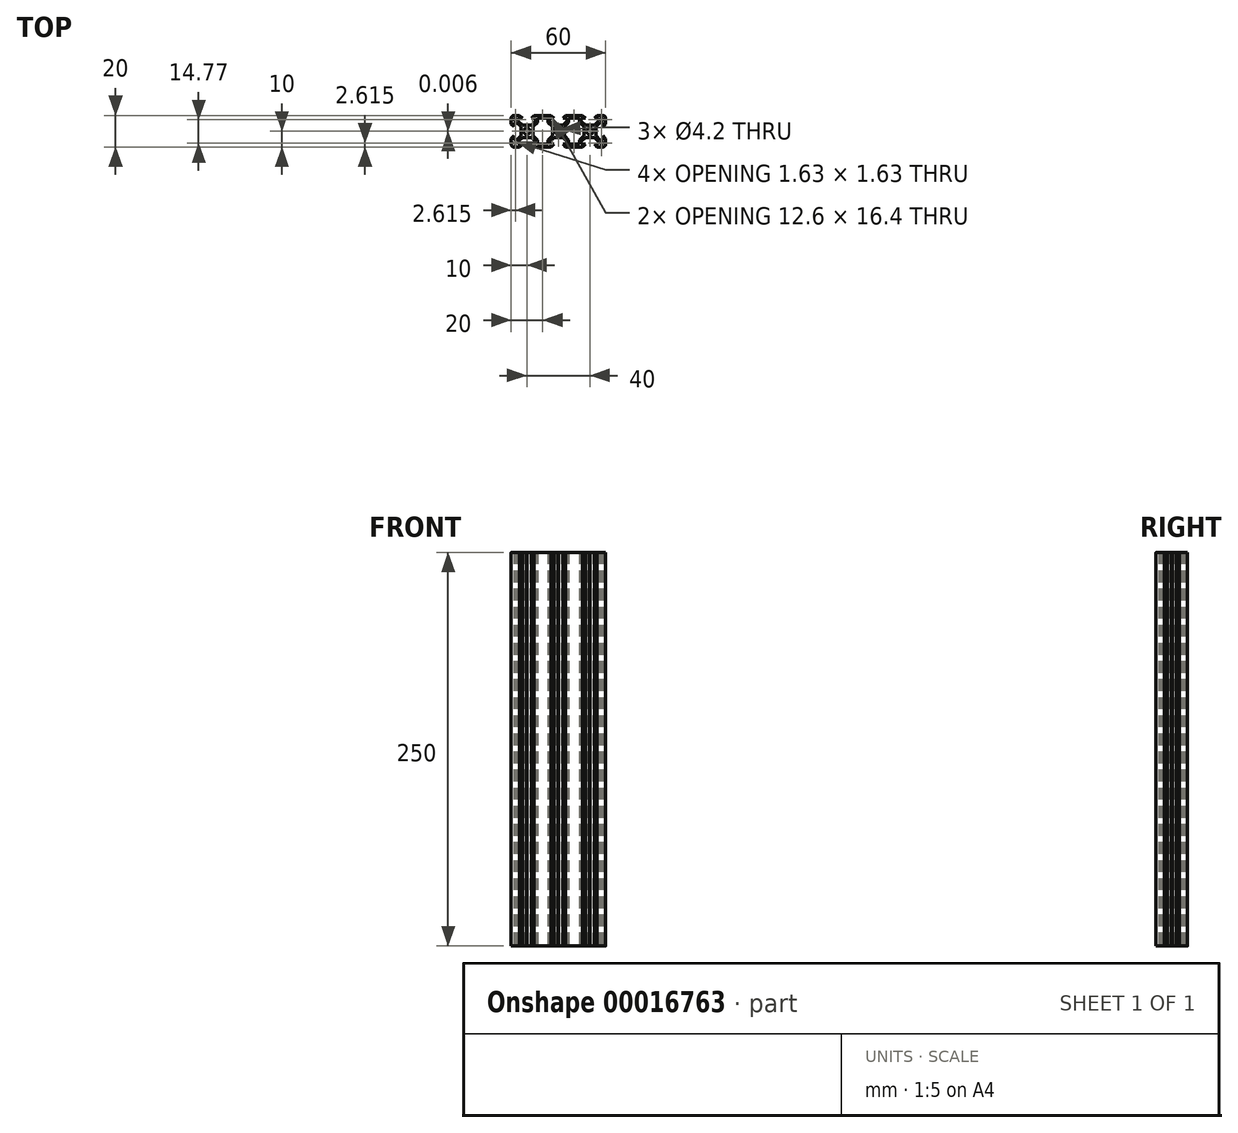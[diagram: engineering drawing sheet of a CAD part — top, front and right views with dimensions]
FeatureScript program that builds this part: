
annotation { "Feature Type Name" : "Feature", "Feature Type Description" : "" }
export const myFeature = defineFeature(function(context is Context, id is Id, definition is map)
    precondition{}
    {
        {
            var Q0;
            Q0=qCreatedBy(makeId("Top.planeOp"),FACE);
            var sketch = newSketch(context, id + "F0", { "sketchPlane" : qUnion([Q0])});
            skCircle(sketch, "E0", {"center": v(20, 0) * mm, "radius": 2.1 * mm});
            skLineSegment(sketch, "E1", {"start": v(-16.1, -2.84) * mm, "end": v(-13.43, -5.5) * mm});
            skLineSegment(sketch, "E2", {"start": v(-16.1, -0.2) * mm, "end": v(-16.1, -2.84) * mm});
            skLineSegment(sketch, "E3", {"start": v(-16.3, 0) * mm, "end": v(-16.1, -0.2) * mm});
            skLineSegment(sketch, "E4", {"start": v(-16.1, 0.2) * mm, "end": v(-16.3, 0) * mm});
            skLineSegment(sketch, "E5", {"start": v(-16.1, 2.84) * mm, "end": v(-16.1, 0.2) * mm});
            skLineSegment(sketch, "E6", {"start": v(-13.43, 5.5) * mm, "end": v(-16.1, 2.84) * mm});
            skLineSegment(sketch, "E7", {"start": v(-13.43, 8.2) * mm, "end": v(-13.43, 5.5) * mm});
            skLineSegment(sketch, "E8", {"start": v(-6.57, 8.2) * mm, "end": v(-13.43, 8.2) * mm});
            skLineSegment(sketch, "E9", {"start": v(-6.57, 5.5) * mm, "end": v(-6.57, 8.2) * mm});
            skLineSegment(sketch, "E10", {"start": v(-3.9, 2.84) * mm, "end": v(-6.57, 5.5) * mm});
            skLineSegment(sketch, "E11", {"start": v(-3.9, 0.2) * mm, "end": v(-3.9, 2.84) * mm});
            skLineSegment(sketch, "E12", {"start": v(-3.7, 0) * mm, "end": v(-3.9, 0.2) * mm});
            skLineSegment(sketch, "E13", {"start": v(-3.9, -0.2) * mm, "end": v(-3.7, 0) * mm});
            skLineSegment(sketch, "E14", {"start": v(-3.9, -2.84) * mm, "end": v(-3.9, -0.2) * mm});
            skLineSegment(sketch, "E15", {"start": v(-6.57, -5.5) * mm, "end": v(-3.9, -2.84) * mm});
            skLineSegment(sketch, "E16", {"start": v(-6.57, -8.2) * mm, "end": v(-6.57, -5.5) * mm});
            skLineSegment(sketch, "E17", {"start": v(-13.43, -8.2) * mm, "end": v(-6.57, -8.2) * mm});
            skLineSegment(sketch, "E18", {"start": v(-13.43, -5.5) * mm, "end": v(-13.43, -8.2) * mm});
            skLineSegment(sketch, "E19", {"start": v(26.57, 7.66) * mm, "end": v(27.66, 6.57) * mm});
            skLineSegment(sketch, "E20", {"start": v(26.57, 8.2) * mm, "end": v(26.57, 7.66) * mm});
            skLineSegment(sketch, "E21", {"start": v(28.2, 8.2) * mm, "end": v(26.57, 8.2) * mm});
            skLineSegment(sketch, "E22", {"start": v(28.2, 6.57) * mm, "end": v(28.2, 8.2) * mm});
            skLineSegment(sketch, "E23", {"start": v(27.66, 6.57) * mm, "end": v(28.2, 6.57) * mm});
            skLineSegment(sketch, "E24", {"start": v(27.66, -6.57) * mm, "end": v(26.57, -7.66) * mm});
            skLineSegment(sketch, "E25", {"start": v(28.2, -6.57) * mm, "end": v(27.66, -6.57) * mm});
            skLineSegment(sketch, "E26", {"start": v(28.2, -8.2) * mm, "end": v(28.2, -6.57) * mm});
            skLineSegment(sketch, "E27", {"start": v(26.57, -8.2) * mm, "end": v(28.2, -8.2) * mm});
            skLineSegment(sketch, "E28", {"start": v(26.57, -7.66) * mm, "end": v(26.57, -8.2) * mm});
            skLineSegment(sketch, "E29", {"start": v(-26.57, -7.66) * mm, "end": v(-27.66, -6.57) * mm});
            skLineSegment(sketch, "E30", {"start": v(-26.57, -8.2) * mm, "end": v(-26.57, -7.66) * mm});
            skLineSegment(sketch, "E31", {"start": v(-28.2, -8.2) * mm, "end": v(-26.57, -8.2) * mm});
            skLineSegment(sketch, "E32", {"start": v(-28.2, -6.57) * mm, "end": v(-28.2, -8.2) * mm});
            skLineSegment(sketch, "E33", {"start": v(-27.66, -6.57) * mm, "end": v(-28.2, -6.57) * mm});
            skLineSegment(sketch, "E34", {"start": v(-27.66, 6.57) * mm, "end": v(-26.57, 7.66) * mm});
            skLineSegment(sketch, "E35", {"start": v(-28.2, 6.57) * mm, "end": v(-27.66, 6.57) * mm});
            skLineSegment(sketch, "E36", {"start": v(-28.2, 8.2) * mm, "end": v(-28.2, 6.57) * mm});
            skLineSegment(sketch, "E37", {"start": v(-26.57, 8.2) * mm, "end": v(-28.2, 8.2) * mm});
            skLineSegment(sketch, "E38", {"start": v(-26.57, 7.66) * mm, "end": v(-26.57, 8.2) * mm});
            skLineSegment(sketch, "E39", {"start": v(-25.5, 8.2) * mm, "end": v(-22.84, 8.2) * mm});
            skLineSegment(sketch, "E40", {"start": v(-22.84, 8.2) * mm, "end": v(-24.64, 10) * mm});
            skLineSegment(sketch, "E41", {"start": v(-24.64, 10) * mm, "end": v(-28.2, 10) * mm});
            skArc(sketch, "E42", {"start": v(-28.2, 10) * mm, "mid": v(-29.47, 9.47) * mm, "end": v(-30, 8.2) * mm});
            skLineSegment(sketch, "E43", {"start": v(-30, 8.2) * mm, "end": v(-30, 4.64) * mm});
            skLineSegment(sketch, "E44", {"start": v(-30, 4.64) * mm, "end": v(-28.2, 2.84) * mm});
            skLineSegment(sketch, "E45", {"start": v(-28.2, 2.84) * mm, "end": v(-28.2, 5.5) * mm});
            skLineSegment(sketch, "E46", {"start": v(-28.2, 5.5) * mm, "end": v(-26.56, 5.5) * mm});
            skLineSegment(sketch, "E47", {"start": v(-26.56, 5.5) * mm, "end": v(-23.9, 2.84) * mm});
            skLineSegment(sketch, "E48", {"start": v(-23.9, 2.84) * mm, "end": v(-23.9, 0.2) * mm});
            skLineSegment(sketch, "E49", {"start": v(-23.9, 0.2) * mm, "end": v(-23.7, 0) * mm});
            skLineSegment(sketch, "E50", {"start": v(-23.7, 0) * mm, "end": v(-23.9, -0.2) * mm});
            skLineSegment(sketch, "E51", {"start": v(-23.9, -0.2) * mm, "end": v(-23.9, -2.84) * mm});
            skLineSegment(sketch, "E52", {"start": v(-23.9, -2.84) * mm, "end": v(-26.56, -5.5) * mm});
            skLineSegment(sketch, "E53", {"start": v(-26.56, -5.5) * mm, "end": v(-28.2, -5.5) * mm});
            skLineSegment(sketch, "E54", {"start": v(-28.2, -5.5) * mm, "end": v(-28.2, -2.84) * mm});
            skLineSegment(sketch, "E55", {"start": v(-28.2, -2.84) * mm, "end": v(-30, -4.64) * mm});
            skLineSegment(sketch, "E56", {"start": v(-30, -4.64) * mm, "end": v(-30, -8.2) * mm});
            skArc(sketch, "E57", {"start": v(-30, -8.2) * mm, "mid": v(-29.47, -9.47) * mm, "end": v(-28.2, -10) * mm});
            skLineSegment(sketch, "E58", {"start": v(-28.2, -10) * mm, "end": v(-24.64, -10) * mm});
            skLineSegment(sketch, "E59", {"start": v(-24.64, -10) * mm, "end": v(-22.84, -8.2) * mm});
            skLineSegment(sketch, "E60", {"start": v(-22.84, -8.2) * mm, "end": v(-25.5, -8.2) * mm});
            skLineSegment(sketch, "E61", {"start": v(-25.5, -8.2) * mm, "end": v(-25.5, -6.56) * mm});
            skLineSegment(sketch, "E62", {"start": v(-25.5, -6.56) * mm, "end": v(-22.84, -3.9) * mm});
            skLineSegment(sketch, "E63", {"start": v(-22.84, -3.9) * mm, "end": v(-20.2, -3.9) * mm});
            skLineSegment(sketch, "E64", {"start": v(-20.2, -3.9) * mm, "end": v(-20, -3.7) * mm});
            skLineSegment(sketch, "E65", {"start": v(-20, -3.7) * mm, "end": v(-19.8, -3.9) * mm});
            skLineSegment(sketch, "E66", {"start": v(-19.8, -3.9) * mm, "end": v(-17.16, -3.9) * mm});
            skLineSegment(sketch, "E67", {"start": v(-17.16, -3.9) * mm, "end": v(-14.5, -6.56) * mm});
            skLineSegment(sketch, "E68", {"start": v(-14.5, -6.56) * mm, "end": v(-14.5, -8.2) * mm});
            skLineSegment(sketch, "E69", {"start": v(-14.5, -8.2) * mm, "end": v(-17.16, -8.2) * mm});
            skLineSegment(sketch, "E70", {"start": v(-17.16, -8.2) * mm, "end": v(-15.36, -10) * mm});
            skLineSegment(sketch, "E71", {"start": v(-15.36, -10) * mm, "end": v(-4.64, -10) * mm});
            skLineSegment(sketch, "E72", {"start": v(-4.64, -10) * mm, "end": v(-2.84, -8.2) * mm});
            skLineSegment(sketch, "E73", {"start": v(-2.84, -8.2) * mm, "end": v(-5.5, -8.2) * mm});
            skLineSegment(sketch, "E74", {"start": v(-5.5, -8.2) * mm, "end": v(-5.5, -6.56) * mm});
            skLineSegment(sketch, "E75", {"start": v(-5.5, -6.56) * mm, "end": v(-2.84, -3.9) * mm});
            skLineSegment(sketch, "E76", {"start": v(-2.84, -3.9) * mm, "end": v(-0.2, -3.9) * mm});
            skLineSegment(sketch, "E77", {"start": v(-0.2, -3.9) * mm, "end": v(0, -3.7) * mm});
            skLineSegment(sketch, "E78", {"start": v(0, -3.7) * mm, "end": v(0.2, -3.9) * mm});
            skLineSegment(sketch, "E79", {"start": v(0.2, -3.9) * mm, "end": v(2.84, -3.9) * mm});
            skLineSegment(sketch, "E80", {"start": v(2.84, -3.9) * mm, "end": v(5.5, -6.56) * mm});
            skLineSegment(sketch, "E81", {"start": v(5.5, -6.56) * mm, "end": v(5.5, -8.2) * mm});
            skLineSegment(sketch, "E82", {"start": v(5.5, -8.2) * mm, "end": v(2.84, -8.2) * mm});
            skLineSegment(sketch, "E83", {"start": v(2.84, -8.2) * mm, "end": v(4.64, -10) * mm});
            skLineSegment(sketch, "E84", {"start": v(4.64, -10) * mm, "end": v(15.36, -10) * mm});
            skLineSegment(sketch, "E85", {"start": v(15.36, -10) * mm, "end": v(17.16, -8.2) * mm});
            skLineSegment(sketch, "E86", {"start": v(17.16, -8.2) * mm, "end": v(14.5, -8.2) * mm});
            skLineSegment(sketch, "E87", {"start": v(14.5, -8.2) * mm, "end": v(14.5, -6.56) * mm});
            skLineSegment(sketch, "E88", {"start": v(14.5, -6.56) * mm, "end": v(17.16, -3.9) * mm});
            skLineSegment(sketch, "E89", {"start": v(17.16, -3.9) * mm, "end": v(19.8, -3.9) * mm});
            skLineSegment(sketch, "E90", {"start": v(19.8, -3.9) * mm, "end": v(20, -3.7) * mm});
            skLineSegment(sketch, "E91", {"start": v(20, -3.7) * mm, "end": v(20.2, -3.9) * mm});
            skLineSegment(sketch, "E92", {"start": v(20.2, -3.9) * mm, "end": v(22.84, -3.9) * mm});
            skLineSegment(sketch, "E93", {"start": v(22.84, -3.9) * mm, "end": v(25.5, -6.56) * mm});
            skLineSegment(sketch, "E94", {"start": v(25.5, -6.56) * mm, "end": v(25.5, -8.2) * mm});
            skLineSegment(sketch, "E95", {"start": v(25.5, -8.2) * mm, "end": v(22.84, -8.2) * mm});
            skLineSegment(sketch, "E96", {"start": v(22.84, -8.2) * mm, "end": v(24.64, -10) * mm});
            skLineSegment(sketch, "E97", {"start": v(24.64, -10) * mm, "end": v(28.2, -10) * mm});
            skArc(sketch, "E98", {"start": v(28.2, -10) * mm, "mid": v(29.47, -9.47) * mm, "end": v(30, -8.2) * mm});
            skLineSegment(sketch, "E99", {"start": v(30, -8.2) * mm, "end": v(30, -4.64) * mm});
            skLineSegment(sketch, "E100", {"start": v(30, -4.64) * mm, "end": v(28.2, -2.84) * mm});
            skLineSegment(sketch, "E101", {"start": v(28.2, -2.84) * mm, "end": v(28.2, -5.5) * mm});
            skLineSegment(sketch, "E102", {"start": v(28.2, -5.5) * mm, "end": v(26.56, -5.5) * mm});
            skLineSegment(sketch, "E103", {"start": v(26.56, -5.5) * mm, "end": v(23.9, -2.84) * mm});
            skLineSegment(sketch, "E104", {"start": v(23.9, -2.84) * mm, "end": v(23.9, -0.2) * mm});
            skLineSegment(sketch, "E105", {"start": v(23.9, -0.2) * mm, "end": v(23.7, 0) * mm});
            skLineSegment(sketch, "E106", {"start": v(23.7, 0) * mm, "end": v(23.9, 0.2) * mm});
            skLineSegment(sketch, "E107", {"start": v(23.9, 0.2) * mm, "end": v(23.9, 2.84) * mm});
            skLineSegment(sketch, "E108", {"start": v(23.9, 2.84) * mm, "end": v(26.56, 5.5) * mm});
            skLineSegment(sketch, "E109", {"start": v(26.56, 5.5) * mm, "end": v(28.2, 5.5) * mm});
            skLineSegment(sketch, "E110", {"start": v(28.2, 5.5) * mm, "end": v(28.2, 2.84) * mm});
            skLineSegment(sketch, "E111", {"start": v(28.2, 2.84) * mm, "end": v(30, 4.64) * mm});
            skLineSegment(sketch, "E112", {"start": v(30, 4.64) * mm, "end": v(30, 8.2) * mm});
            skArc(sketch, "E113", {"start": v(30, 8.2) * mm, "mid": v(29.47, 9.47) * mm, "end": v(28.2, 10) * mm});
            skLineSegment(sketch, "E114", {"start": v(28.2, 10) * mm, "end": v(24.64, 10) * mm});
            skLineSegment(sketch, "E115", {"start": v(24.64, 10) * mm, "end": v(22.84, 8.2) * mm});
            skLineSegment(sketch, "E116", {"start": v(22.84, 8.2) * mm, "end": v(25.5, 8.2) * mm});
            skLineSegment(sketch, "E117", {"start": v(25.5, 8.2) * mm, "end": v(25.5, 6.56) * mm});
            skLineSegment(sketch, "E118", {"start": v(25.5, 6.56) * mm, "end": v(22.84, 3.9) * mm});
            skLineSegment(sketch, "E119", {"start": v(22.84, 3.9) * mm, "end": v(20.2, 3.9) * mm});
            skLineSegment(sketch, "E120", {"start": v(20.2, 3.9) * mm, "end": v(20, 3.7) * mm});
            skLineSegment(sketch, "E121", {"start": v(20, 3.7) * mm, "end": v(19.8, 3.9) * mm});
            skLineSegment(sketch, "E122", {"start": v(19.8, 3.9) * mm, "end": v(17.16, 3.9) * mm});
            skLineSegment(sketch, "E123", {"start": v(17.16, 3.9) * mm, "end": v(14.5, 6.56) * mm});
            skLineSegment(sketch, "E124", {"start": v(14.5, 6.56) * mm, "end": v(14.5, 8.2) * mm});
            skLineSegment(sketch, "E125", {"start": v(14.5, 8.2) * mm, "end": v(17.16, 8.2) * mm});
            skLineSegment(sketch, "E126", {"start": v(17.16, 8.2) * mm, "end": v(15.36, 10) * mm});
            skLineSegment(sketch, "E127", {"start": v(15.36, 10) * mm, "end": v(4.64, 10) * mm});
            skLineSegment(sketch, "E128", {"start": v(4.64, 10) * mm, "end": v(2.84, 8.2) * mm});
            skLineSegment(sketch, "E129", {"start": v(2.84, 8.2) * mm, "end": v(5.5, 8.2) * mm});
            skLineSegment(sketch, "E130", {"start": v(5.5, 8.2) * mm, "end": v(5.5, 6.56) * mm});
            skLineSegment(sketch, "E131", {"start": v(5.5, 6.56) * mm, "end": v(2.84, 3.9) * mm});
            skLineSegment(sketch, "E132", {"start": v(2.84, 3.9) * mm, "end": v(0.2, 3.9) * mm});
            skLineSegment(sketch, "E133", {"start": v(0.2, 3.9) * mm, "end": v(0, 3.7) * mm});
            skLineSegment(sketch, "E134", {"start": v(0, 3.7) * mm, "end": v(-0.2, 3.9) * mm});
            skLineSegment(sketch, "E135", {"start": v(-0.2, 3.9) * mm, "end": v(-2.84, 3.9) * mm});
            skLineSegment(sketch, "E136", {"start": v(-2.84, 3.9) * mm, "end": v(-5.5, 6.56) * mm});
            skLineSegment(sketch, "E137", {"start": v(-5.5, 6.56) * mm, "end": v(-5.5, 8.2) * mm});
            skLineSegment(sketch, "E138", {"start": v(-5.5, 8.2) * mm, "end": v(-2.84, 8.2) * mm});
            skLineSegment(sketch, "E139", {"start": v(-2.84, 8.2) * mm, "end": v(-4.64, 10) * mm});
            skLineSegment(sketch, "E140", {"start": v(-4.64, 10) * mm, "end": v(-15.36, 10) * mm});
            skLineSegment(sketch, "E141", {"start": v(-15.36, 10) * mm, "end": v(-17.16, 8.2) * mm});
            skLineSegment(sketch, "E142", {"start": v(-17.16, 8.2) * mm, "end": v(-14.5, 8.2) * mm});
            skLineSegment(sketch, "E143", {"start": v(-14.5, 8.2) * mm, "end": v(-14.5, 6.56) * mm});
            skLineSegment(sketch, "E144", {"start": v(-14.5, 6.56) * mm, "end": v(-17.16, 3.9) * mm});
            skLineSegment(sketch, "E145", {"start": v(-17.16, 3.9) * mm, "end": v(-19.8, 3.9) * mm});
            skLineSegment(sketch, "E146", {"start": v(-19.8, 3.9) * mm, "end": v(-20, 3.7) * mm});
            skLineSegment(sketch, "E147", {"start": v(-20, 3.7) * mm, "end": v(-20.2, 3.9) * mm});
            skLineSegment(sketch, "E148", {"start": v(-20.2, 3.9) * mm, "end": v(-22.84, 3.9) * mm});
            skLineSegment(sketch, "E149", {"start": v(-22.84, 3.9) * mm, "end": v(-25.5, 6.56) * mm});
            skLineSegment(sketch, "E150", {"start": v(-25.5, 6.56) * mm, "end": v(-25.5, 8.2) * mm});
            skCircle(sketch, "E151", {"center": v(-20, 0) * mm, "radius": 2.1 * mm});
            skLineSegment(sketch, "E152", {"start": v(16.1, 0.2) * mm, "end": v(16.1, 2.84) * mm});
            skLineSegment(sketch, "E153", {"start": v(16.3, 0) * mm, "end": v(16.1, 0.2) * mm});
            skLineSegment(sketch, "E154", {"start": v(16.1, -0.2) * mm, "end": v(16.3, 0) * mm});
            skLineSegment(sketch, "E155", {"start": v(16.1, -2.84) * mm, "end": v(16.1, -0.2) * mm});
            skLineSegment(sketch, "E156", {"start": v(13.43, -5.5) * mm, "end": v(16.1, -2.84) * mm});
            skLineSegment(sketch, "E157", {"start": v(13.43, -8.2) * mm, "end": v(13.43, -5.5) * mm});
            skLineSegment(sketch, "E158", {"start": v(6.57, -8.2) * mm, "end": v(13.43, -8.2) * mm});
            skLineSegment(sketch, "E159", {"start": v(6.57, -5.5) * mm, "end": v(6.57, -8.2) * mm});
            skLineSegment(sketch, "E160", {"start": v(3.9, -2.84) * mm, "end": v(6.57, -5.5) * mm});
            skLineSegment(sketch, "E161", {"start": v(3.9, -0.2) * mm, "end": v(3.9, -2.84) * mm});
            skLineSegment(sketch, "E162", {"start": v(3.7, 0) * mm, "end": v(3.9, -0.2) * mm});
            skLineSegment(sketch, "E163", {"start": v(3.9, 0.2) * mm, "end": v(3.7, 0) * mm});
            skLineSegment(sketch, "E164", {"start": v(3.9, 2.84) * mm, "end": v(3.9, 0.2) * mm});
            skLineSegment(sketch, "E165", {"start": v(6.57, 5.5) * mm, "end": v(3.9, 2.84) * mm});
            skLineSegment(sketch, "E166", {"start": v(6.57, 8.2) * mm, "end": v(6.57, 5.5) * mm});
            skLineSegment(sketch, "E167", {"start": v(13.43, 8.2) * mm, "end": v(6.57, 8.2) * mm});
            skLineSegment(sketch, "E168", {"start": v(13.43, 5.5) * mm, "end": v(13.43, 8.2) * mm});
            skLineSegment(sketch, "E169", {"start": v(16.1, 2.84) * mm, "end": v(13.43, 5.5) * mm});
            skCircle(sketch, "E170", {"center": v(0, 0) * mm, "radius": 2.1 * mm});
            skSolve(sketch);
        }
        {
            var Q0;
            Q0 = qSketchRegion(id + "F0", true);
            extrude(context, id + "F1", {"entities" : qUnion([Q0]), "depth" : 250 * mm});
        }
    });
